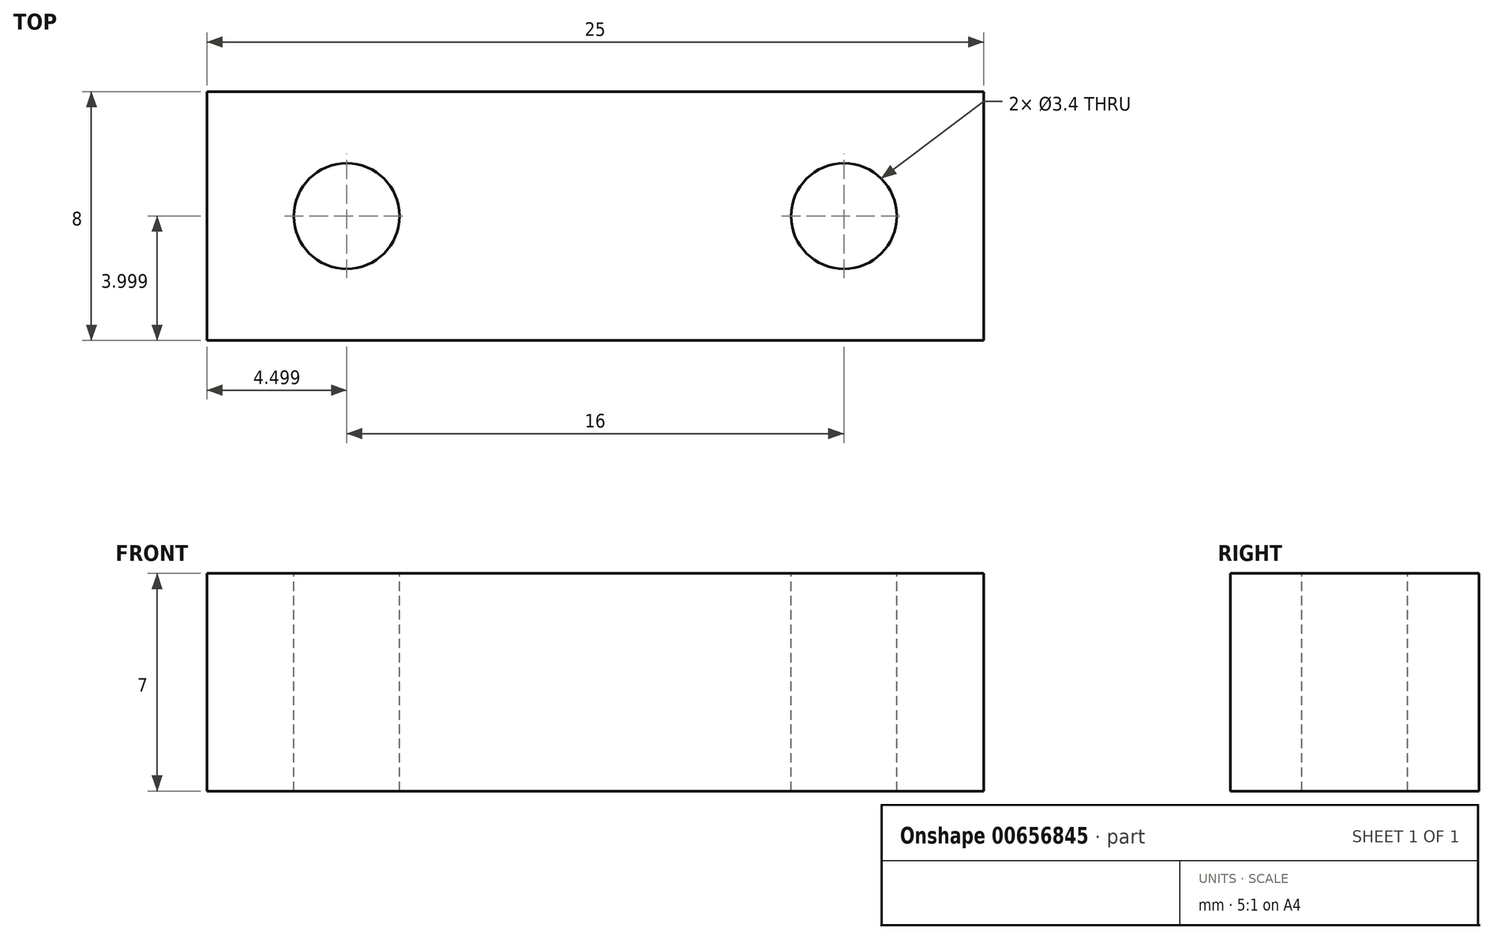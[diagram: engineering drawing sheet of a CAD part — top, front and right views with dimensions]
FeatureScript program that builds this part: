
annotation { "Feature Type Name" : "Feature", "Feature Type Description" : "" }
export const myFeature = defineFeature(function(context is Context, id is Id, definition is map)
    precondition{}
    {
        {
            var Q0;
            Q0=qCreatedBy(makeId("Top.planeOp"),FACE);
            var sketch = newSketch(context, id + "F0", { "sketchPlane" : qUnion([Q0])});
            skLineSegment(sketch, "E0.bottom", {"start": v(3.87, -3.34) * mm, "end": v(28.87, -3.34) * mm});
            skLineSegment(sketch, "E0.top", {"start": v(3.87, -11.34) * mm, "end": v(28.87, -11.34) * mm});
            skLineSegment(sketch, "E0.left", {"start": v(3.87, -3.34) * mm, "end": v(3.87, -11.34) * mm});
            skLineSegment(sketch, "E0.right", {"start": v(28.87, -3.34) * mm, "end": v(28.87, -11.34) * mm});
            skSolve(sketch);
        }
        {
            var Q0;
            Q0=makeQuery(id+"F0.imprint","IMPRINT",FACE,{"disambiguationData":[TD([[makeQuery(id+"F0.imprint","IMPRINT",EDGE,{"derivedFrom":sQuery(id+"F0.wireOp",EDGE,"E0.bottom")}),-1.0]])]});
            extrude(context, id + "F1", {"entities" : qUnion([Q0]), "depth" : 7 * mm, "offsetDistance" : 25 * mm});
        }
        {
            var Q0;
            Q0=makeQuery(id+"F1.opExtrude","CAP_FACE",FACE,{"disambiguationData":[OSD([sQuery(id+"F0.wireOp",EDGE,"E0.bottom"),sQuery(id+"F0.wireOp",EDGE,"E0.top"),sQuery(id+"F0.wireOp",EDGE,"E0.left"),sQuery(id+"F0.wireOp",EDGE,"E0.right")])],"isStart":false});
            var sketch = newSketch(context, id + "F2", { "sketchPlane" : qUnion([Q0])});
            skLineSegment(sketch, "E1", {"start": v(3.87, -7.34) * mm, "end": v(28.87, -7.34) * mm});
            skLineSegment(sketch, "E2", {"start": v(16.37, -3.34) * mm, "end": v(16.37, -11.34) * mm});
            skPoint(sketch, "E3", {"position": v(8.37, -7.34) * mm});
            skPoint(sketch, "E4.MirrorP", {"position": v(24.37, -7.34) * mm});
            skSolve(sketch);
        }
        {
            var Q0;
            Q0=sQuery(id+"F2.wireOp",VERTEX,"E3");
            var Q1;
            Q1=sQuery(id+"F2.wireOp",VERTEX,"E4.MirrorP");
            var Q2;
            Q2=makeQuery(id+"F1.opExtrude","SWEPT_BODY",BODY,{"disambiguationData":[OSD([sQuery(id+"F0.wireOp",EDGE,"E0.bottom"),sQuery(id+"F0.wireOp",EDGE,"E0.top"),sQuery(id+"F0.wireOp",EDGE,"E0.left"),sQuery(id+"F0.wireOp",EDGE,"E0.right")])]});
            hole(context, id + "F3", {"style" : HoleStyle.SIMPLE, "endStyle" : HoleEndStyle.THROUGH, "holeDiameter" : 3.4 * mm, "majorDiameter" : 3 * mm, "isTappedThrough" : true, "tappedDepth" : 12 * mm, "tapClearance" : 3, "locations" : qUnion([Q0, Q1]), "scope" : qUnion([Q2])});
        }
    });
